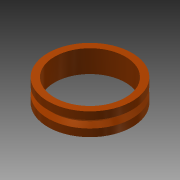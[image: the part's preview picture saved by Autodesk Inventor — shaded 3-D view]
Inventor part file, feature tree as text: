
AUTODESK INVENTOR PART (.ipt)
format: ipt  version: 2013 (Build 170138000, 138)  size: 92,160 bytes
history: native  units: mm
features: revolve x1, sketch x1
ambient origin geometry x8: Origin, YZ Plane, XZ Plane, XY Plane, X Axis, Y Axis, Z Axis, Center Point
bodies: Solid1 (feature_tree)
feature tree (2):
  revolve  "Revolution1"  [1 undecoded]
  sketch  "Sketch1"  dims[d0=11.1mm d3=7.0mm d4=12.0mm d6=90.0deg]
note: 1 required parameter value undecoded (feature->parameter linkage not recoverable at this tier; creation-order binding heuristic only, values carry confidence <= 0.55)
